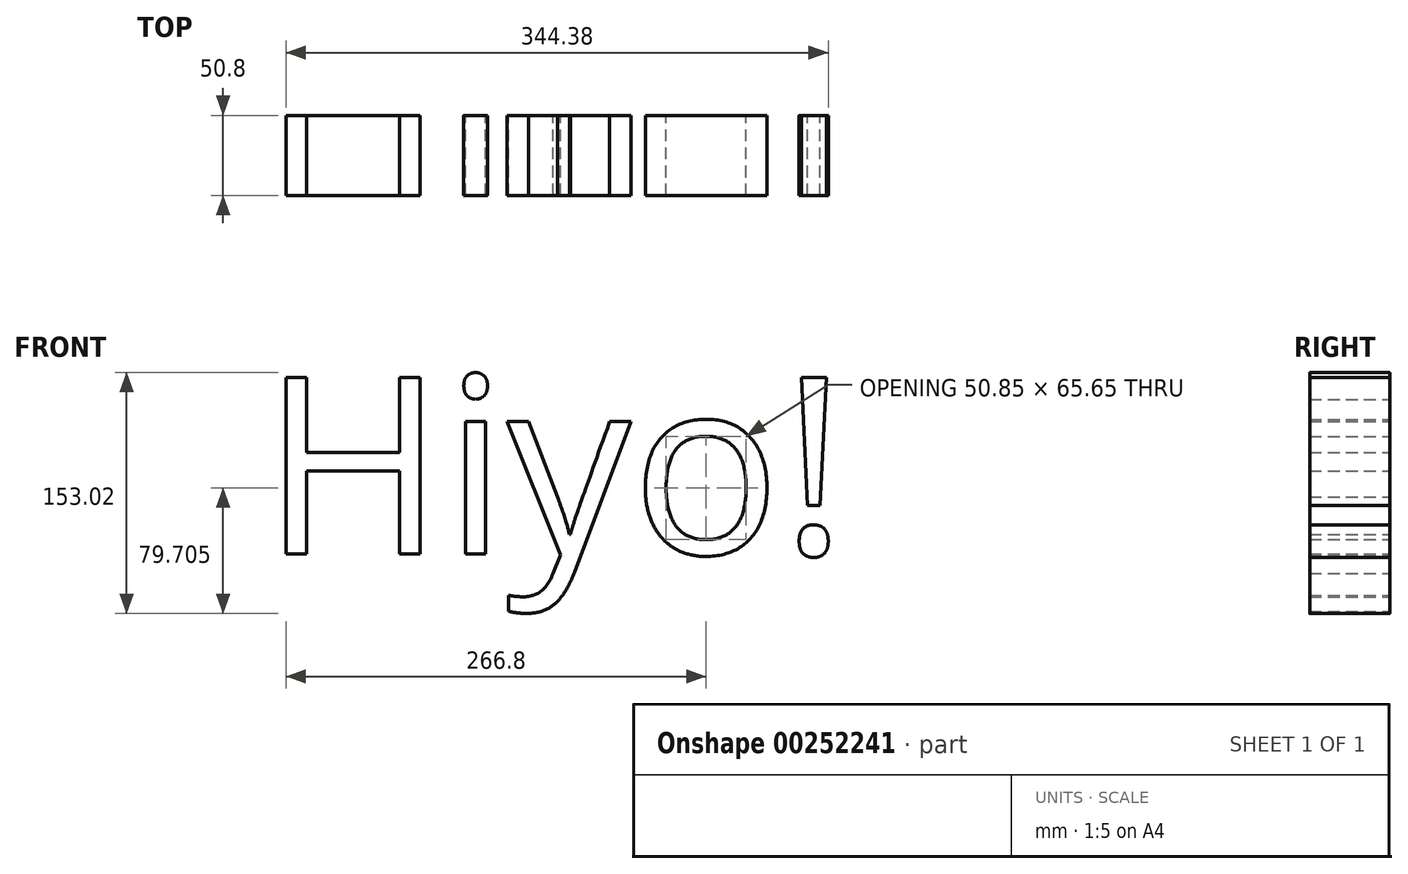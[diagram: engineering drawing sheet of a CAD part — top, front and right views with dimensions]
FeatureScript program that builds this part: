
annotation { "Feature Type Name" : "Feature", "Feature Type Description" : "" }
export const myFeature = defineFeature(function(context is Context, id is Id, definition is map)
    precondition{}
    {
        {
            var Q0;
            Q0=qCreatedBy(makeId("Front.planeOp"),FACE);
            var sketch = newSketch(context, id + "F0", { "sketchPlane" : qUnion([Q0])});
            skText(sketch, "E0", { "text": "Hiyo!", "fontName": "OpenSans-Regular.ttf"});
            const initialGuessF0  = {"E0": [-0.20104, -0.06425, 1, 0, 0.11309]};
            skSetInitialGuess(sketch, initialGuessF0);
            skSolve(sketch);
        }
        {
            var Q0;
            Q0 = qSketchRegion(id + "F0", true);
            extrude(context, id + "F1", {"entities" : qUnion([Q0]), "depth" : 50.8 * mm});
        }
    });
